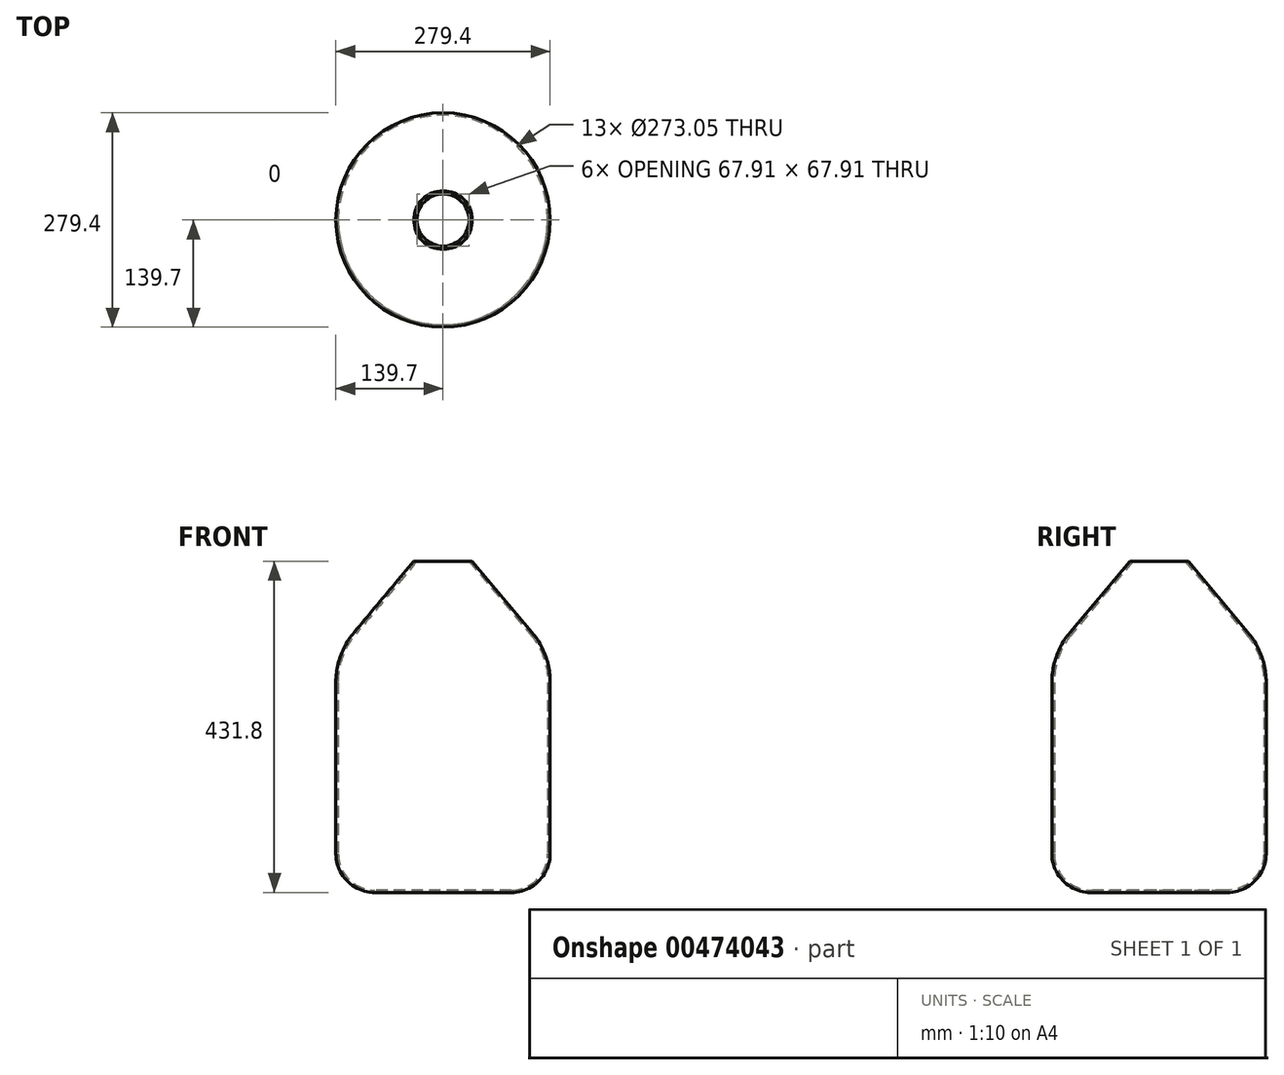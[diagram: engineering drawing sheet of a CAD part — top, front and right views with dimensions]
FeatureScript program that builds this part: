
annotation { "Feature Type Name" : "Feature", "Feature Type Description" : "" }
export const myFeature = defineFeature(function(context is Context, id is Id, definition is map)
    precondition{}
    {
        {
            var Q0;
            Q0=qCreatedBy(makeId("Top.planeOp"),FACE);
            var sketch = newSketch(context, id + "F0", { "sketchPlane" : qUnion([Q0])});
            skCircle(sketch, "E0", {"center": v(0, 0) * mm, "radius": 139.7 * mm});
            skSolve(sketch);
        }
        {
            var Q0;
            Q0=makeQuery(id+"F0.imprint","IMPRINT",FACE,{"disambiguationData":[TD([[makeQuery(id+"F0.imprint","IMPRINT",EDGE,{"derivedFrom":sQuery(id+"F0.wireOp",EDGE,"E0")}),1.0]])]});
            extrude(context, id + "F1", {"entities" : qUnion([Q0]), "depth" : 431.8 * mm});
        }
        {
            var Q0;
            Q0=makeQuery(id+"F1.opExtrude","CAP_EDGE",EDGE,{"disambiguationData":[OSD([sQuery(id+"F0.wireOp",EDGE,"E0")])],"isStart":true});
            fillet(context, id + "F2", {"entities" : qUnion([Q0]), "radius" : 50.8 * mm, "tangentPropagation" : true, "allowEdgeOverflow" : false});
        }
        {
            var Q0;
            Q0=makeQuery(id+"F1.opExtrude","CAP_EDGE",EDGE,{"disambiguationData":[OSD([sQuery(id+"F0.wireOp",EDGE,"E0")])],"isStart":false});
            chamfer(context, id + "F3", {"entities" : qUnion([Q0]), "chamferType" : ChamferType.OFFSET_ANGLE, "width" : 101.6 * mm, "oppositeDirection" : false, "angle" : 50 * degree, "tangentPropagation" : true});
        }
        {
            var Q0;
            {var subQ0=sQuery(id+"F0.wireOp",EDGE,"E0");Q0=makeQuery(id+"F3.opChamfer","BLEND_EDGE",EDGE,{"blendedFrom":[makeQuery(id+"F1.opExtrude","CAP_EDGE",EDGE,{"disambiguationData":[OSD([subQ0])],"isStart":false}),makeQuery(id+"F1.opExtrude","SWEPT_FACE",FACE,{"disambiguationData":[OSD([subQ0])]})],"blendedInto":[makeQuery(id+"F1.opExtrude","SWEPT_FACE",FACE,{"disambiguationData":[OSD([subQ0])]})]});}
            fillet(context, id + "F4", {"entities" : qUnion([Q0]), "radius" : 101.6 * mm, "tangentPropagation" : true, "allowEdgeOverflow" : false});
        }
        {
            var Q0;
            Q0=makeQuery(id+"F1.opExtrude","CAP_FACE",FACE,{"disambiguationData":[OSD([sQuery(id+"F0.wireOp",EDGE,"E0")])],"isStart":false});
            shell(context, id + "F5", {"entities" : qUnion([Q0]), "thickness" : 3.17 * mm});
        }
        {
            var Q0;
            Q0=qCreatedBy(makeId("Front.planeOp"),FACE);
            cPlane(context, id + "F6", {"entities" : qUnion([Q0]), "cplaneType" : CPlaneType.OFFSET, "offset" : 139.7 * mm, "width" : 152.4 * mm, "height" : 152.4 * mm});
        }
    });
